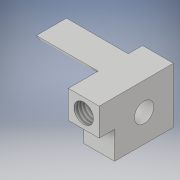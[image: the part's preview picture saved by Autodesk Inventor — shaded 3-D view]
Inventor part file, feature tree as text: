
AUTODESK INVENTOR PART (.ipt)
format: ipt  version: 2019 (Build 230136000, 136)  size: 146,432 bytes
history: native  units: in
note: dims shown in document units (in); Inventor stores cm internally (conversion verified against a paired STEP export)
features: sketch x5, extrude x4, hole x1, thread x1
ambient origin geometry x8: Origin, YZ Plane, XZ Plane, XY Plane, X Axis, Y Axis, Z Axis, Center Point
bodies: Solid1 (feature_tree)
feature tree (11):
  sketch  "Sketch1"  dims[d0=0.4488in d1=0.4764in]
  extrude  "Extrusion1"  Depth=0.4764in
  extrude  "Extrusion2"  Depth=0.1162in
  sketch  "Sketch3"  dims[d2=0.244in d3=0.1162in]
  sketch  "Sketch6"  dims[d4=0.25in d5=0.0in d6=0.5in d7=0.0in]
  hole  "Hole2"  [1 undecoded]
  extrude  "Extrusion8"  Depth=0.4764in
  sketch  "Sketch7"  dims[d19=0.4764in d20=0.2382in]
  extrude  "Extrusion9"  Depth=0.4488in
  thread  "Thread2"  [1 undecoded]
  sketch  "Sketch8"  dims[d29=0.0787in d30=0.4488in d31=0.2244in d33=0.4488in d37=0.1575in d38=0.75in d39=0.119in d40=0.25in d41=0.5635in d42=1.0in d43=0.8108in d46=0.2244in d47=0.125in d48=0.0in d50=0.25in d51=0.2244in d52=0.1122in d53=0.125in d63=0.1122in d64=0.125in d65=0.1575in d66=0.35in d67=0.0in d68=1.0in d69=0.0in d54=1.0in d55=1.0in d56=1.0in d57=0.15in d58=0.25in d59=0.375in d60=0.5635in d61=0.75in d62=0.8108in]
note: 2 required parameter values undecoded (feature->parameter linkage not recoverable at this tier; creation-order binding heuristic only, values carry confidence <= 0.55)
